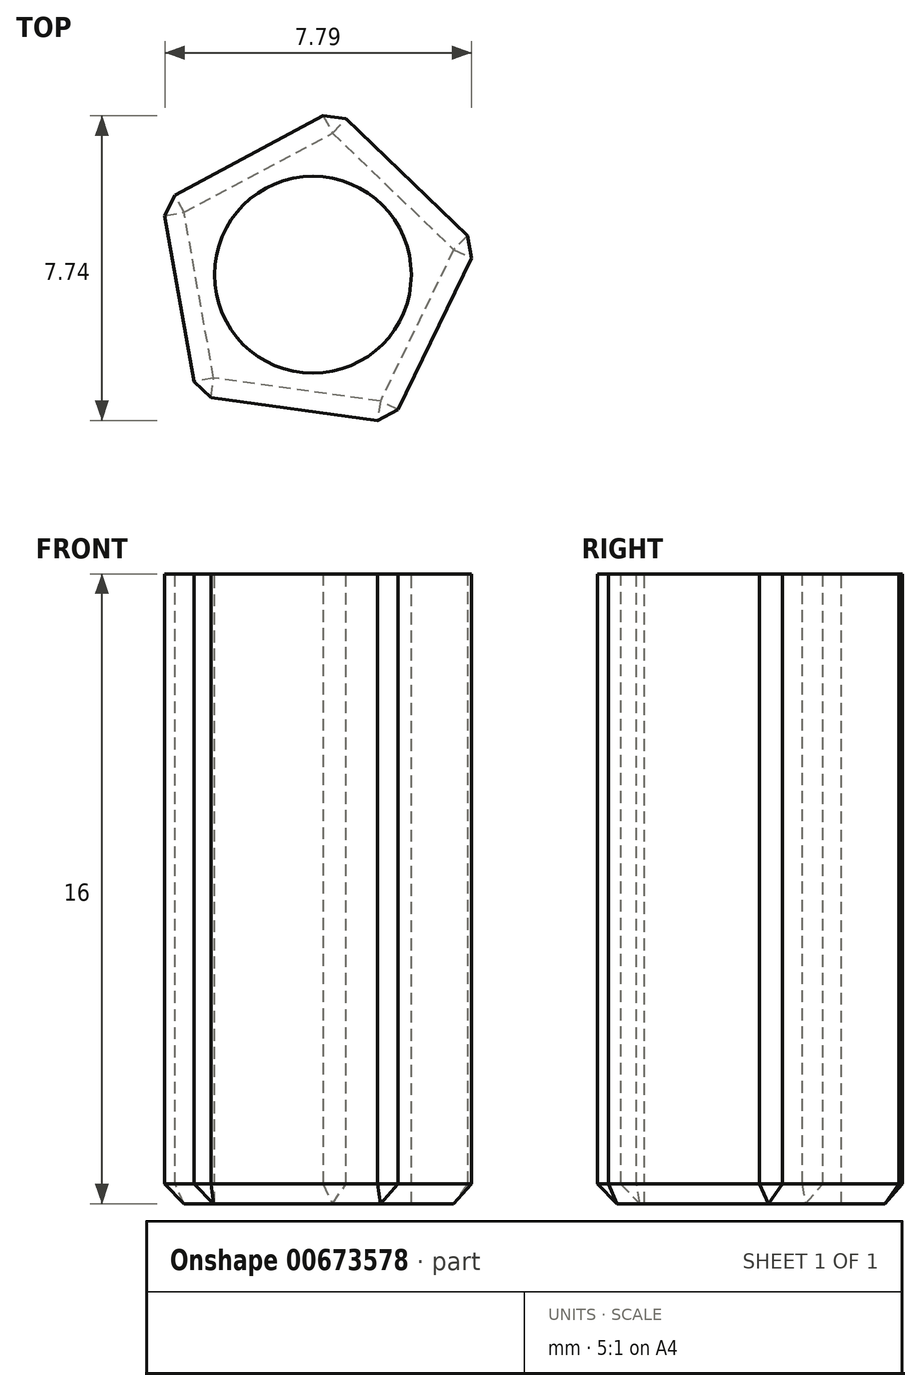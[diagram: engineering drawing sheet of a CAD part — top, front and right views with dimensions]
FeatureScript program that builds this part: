
annotation { "Feature Type Name" : "Feature", "Feature Type Description" : "" }
export const myFeature = defineFeature(function(context is Context, id is Id, definition is map)
    precondition{}
    {
        {
            var Q0;
            Q0=qCreatedBy(makeId("Top.planeOp"),FACE);
            var sketch = newSketch(context, id + "F0", { "sketchPlane" : qUnion([Q0])});
            skCircle(sketch, "E0.cCircle", {"center": v(0, 0) * mm, "radius": 3.44 * mm, "construction": true});
            skLineSegment(sketch, "E0.0", {"start": v(-3.83, 1.86) * mm, "end": v(0.58, 4.21) * mm});
            skLineSegment(sketch, "E0.1", {"start": v(0.58, 4.21) * mm, "end": v(4.19, 0.75) * mm});
            skLineSegment(sketch, "E0.2", {"start": v(4.19, 0.75) * mm, "end": v(2, -3.75) * mm});
            skLineSegment(sketch, "E0.3", {"start": v(2, -3.75) * mm, "end": v(-2.95, -3.07) * mm});
            skLineSegment(sketch, "E0.4", {"start": v(-2.95, -3.07) * mm, "end": v(-3.83, 1.86) * mm});
            skPoint(sketch, "E0.0.midPoint", {"position": v(-1.62, 3.04) * mm});
            skCircle(sketch, "E1", {"center": v(0, 0) * mm, "radius": 2.5 * mm});
            skSolve(sketch);
        }
        {
            var Q0;
            Q0=makeQuery(id+"F0.imprint","IMPRINT",FACE,{"disambiguationData":[TD([[makeQuery(id+"F0.imprint","IMPRINT",EDGE,{"derivedFrom":sQuery(id+"F0.wireOp",EDGE,"E0.0")}),-1.0]])]});
            extrude(context, id + "F1", {"entities" : qUnion([Q0]), "oppositeDirection" : true, "depth" : 16 * mm, "offsetDistance" : 25 * mm});
        }
        {
            var Q0;
            Q0=makeQuery(id+"F1.opExtrude","SWEPT_EDGE",EDGE,{"disambiguationData":[OSD([sQuery(id+"F0.wireOp",EDGE,"E0.2"),sQuery(id+"F0.wireOp",EDGE,"E0.3")])]});
            var Q1;
            Q1=makeQuery(id+"F1.opExtrude","SWEPT_EDGE",EDGE,{"disambiguationData":[OSD([sQuery(id+"F0.wireOp",EDGE,"E0.1"),sQuery(id+"F0.wireOp",EDGE,"E0.2")])]});
            var Q2;
            Q2=makeQuery(id+"F1.opExtrude","SWEPT_EDGE",EDGE,{"disambiguationData":[OSD([sQuery(id+"F0.wireOp",EDGE,"E0.3"),sQuery(id+"F0.wireOp",EDGE,"E0.4")])]});
            var Q3;
            Q3=makeQuery(id+"F1.opExtrude","SWEPT_EDGE",EDGE,{"disambiguationData":[OSD([sQuery(id+"F0.wireOp",EDGE,"E0.0"),sQuery(id+"F0.wireOp",EDGE,"E0.1")])]});
            var Q4;
            Q4=makeQuery(id+"F1.opExtrude","SWEPT_EDGE",EDGE,{"disambiguationData":[OSD([sQuery(id+"F0.wireOp",EDGE,"E0.0"),sQuery(id+"F0.wireOp",EDGE,"E0.4")])]});
            var Q5;
            Q5=makeQuery(id+"F1.opExtrude","CAP_EDGE",EDGE,{"disambiguationData":[OSD([sQuery(id+"F0.wireOp",EDGE,"E0.2")])],"isStart":false});
            var Q6;
            Q6=makeQuery(id+"F1.opExtrude","CAP_EDGE",EDGE,{"disambiguationData":[OSD([sQuery(id+"F0.wireOp",EDGE,"E0.4")])],"isStart":false});
            var Q7;
            Q7=makeQuery(id+"F1.opExtrude","CAP_EDGE",EDGE,{"disambiguationData":[OSD([sQuery(id+"F0.wireOp",EDGE,"E0.0")])],"isStart":false});
            var Q8;
            Q8=makeQuery(id+"F1.opExtrude","CAP_EDGE",EDGE,{"disambiguationData":[OSD([sQuery(id+"F0.wireOp",EDGE,"E0.1")])],"isStart":false});
            var Q9;
            Q9=makeQuery(id+"F1.opExtrude","CAP_EDGE",EDGE,{"disambiguationData":[OSD([sQuery(id+"F0.wireOp",EDGE,"E0.3")])],"isStart":false});
            chamfer(context, id + "F2", {"entities" : qUnion([Q0, Q1, Q2, Q3, Q4, Q5, Q6, Q7, Q8, Q9]), "width" : .5 * mm, "tangentPropagation" : true});
        }
    });
